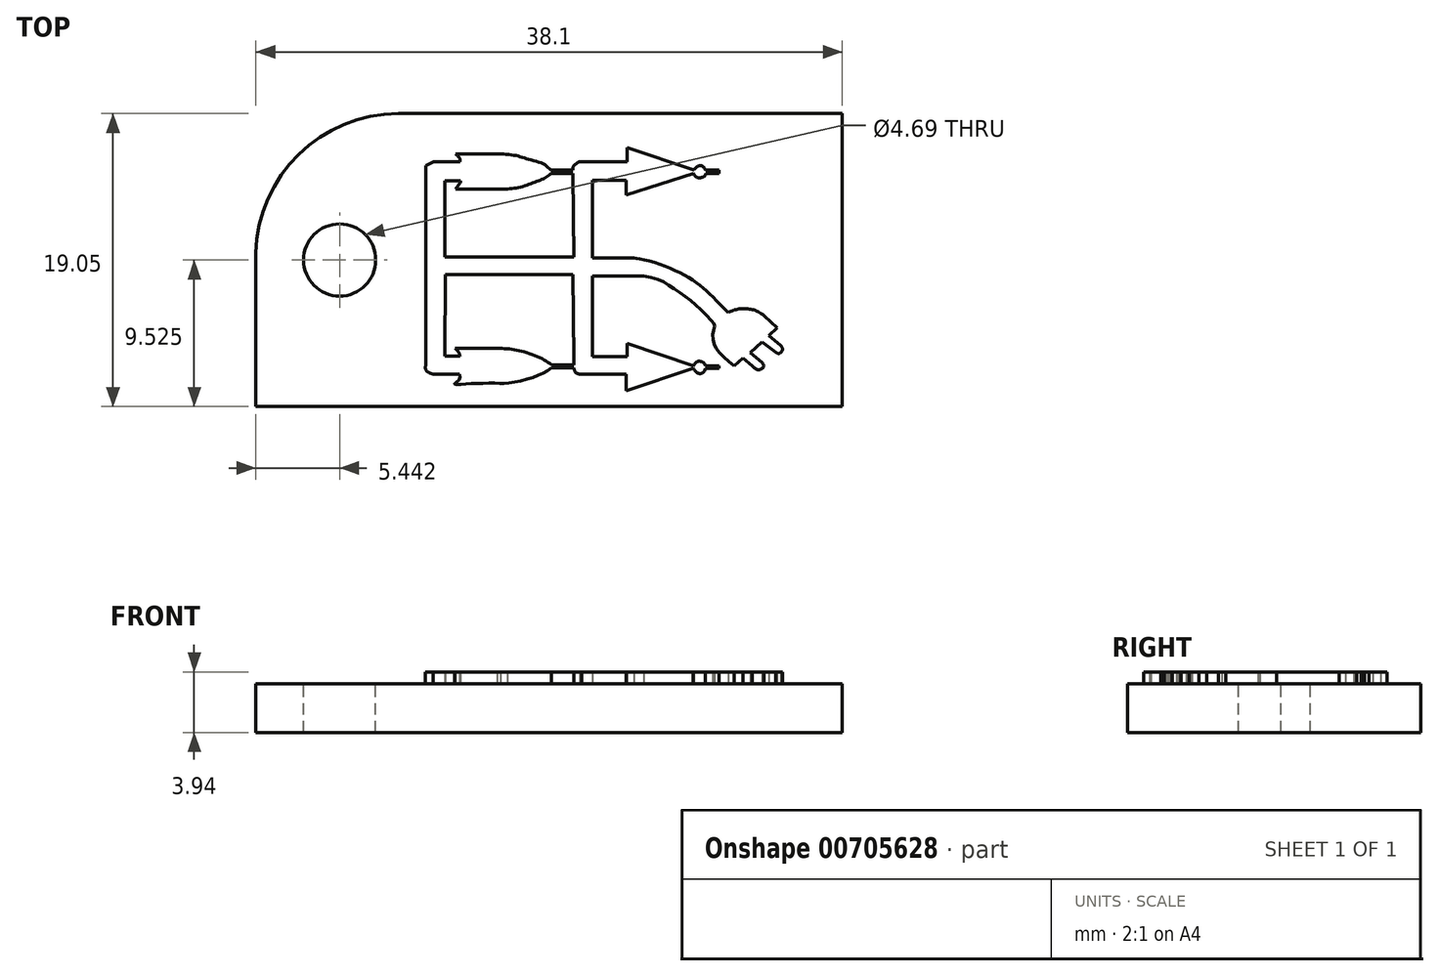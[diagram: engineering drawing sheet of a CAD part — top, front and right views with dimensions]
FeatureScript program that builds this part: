
annotation { "Feature Type Name" : "Feature", "Feature Type Description" : "" }
export const myFeature = defineFeature(function(context is Context, id is Id, definition is map)
    precondition{}
    {
        {
            var Q0;
            Q0=qCreatedBy(makeId("Top.planeOp"),FACE);
            var sketch = newSketch(context, id + "F0", { "sketchPlane" : qUnion([Q0])});
            skLineSegment(sketch, "E0.bottom", {"start": v(0, 0) * mm, "end": v(-38.1, 0) * mm});
            skLineSegment(sketch, "E0.top", {"start": v(0, 19.05) * mm, "end": v(-38.1, 19.05) * mm});
            skLineSegment(sketch, "E0.left", {"start": v(0, 0) * mm, "end": v(0, 19.05) * mm});
            skLineSegment(sketch, "E0.right", {"start": v(-38.1, 0) * mm, "end": v(-38.1, 19.05) * mm});
            skSolve(sketch);
        }
        {
            var Q0;
            Q0=makeQuery(id+"F0.imprint","IMPRINT",FACE,{"disambiguationData":[TD([[makeQuery(id+"F0.imprint","IMPRINT",EDGE,{"derivedFrom":sQuery(id+"F0.wireOp",EDGE,"E0.bottom")}),-1.0]])]});
            extrude(context, id + "F1", {"entities" : qUnion([Q0]), "depth" : 3.17 * mm, "offsetDistance" : 25.4 * mm});
        }
        {
            var Q0;
            Q0=makeQuery(id+"F1.opExtrude","CAP_FACE",FACE,{"disambiguationData":[OSD([sQuery(id+"F0.wireOp",EDGE,"E0.bottom"),sQuery(id+"F0.wireOp",EDGE,"E0.top"),sQuery(id+"F0.wireOp",EDGE,"E0.left"),sQuery(id+"F0.wireOp",EDGE,"E0.right")])],"isStart":false});
            var sketch = newSketch(context, id + "F2", { "sketchPlane" : qUnion([Q0])});
            skLineSegment(sketch, "E1", {"start": v(-38.1, 9.52) * mm, "end": v(0, 9.53) * mm, "construction": true});
            skArc(sketch, "E2", {"start": v(-28.83, 19.05) * mm, "mid": v(-35.46, 16.24) * mm, "end": v(-38.1, 9.52) * mm});
            skArc(sketch, "E3.MirrorCS", {"start": v(-28.83, 0) * mm, "mid": v(-35.46, 2.81) * mm, "end": v(-38.1, 9.52) * mm});
            skCircle(sketch, "E4", {"center": v(-32.66, 9.52) * mm, "radius": 2.35 * mm});
            skSolve(sketch);
        }
        {
            var Q0;
            Q0 = qSketchRegion(id + "F2", true);
            var Q1;
            {var subQ0=sQuery(id+"F2.wireOp",EDGE,"E2");var subQ1=makeQuery(id+"F1.opExtrude","CAP_EDGE",EDGE,{"disambiguationData":[OSD([sQuery(id+"F0.wireOp",EDGE,"E0.top")])],"isStart":false});var subQ2=makeQuery(id+"F2.imprint","INTERSECT",VERTEX,{"derivedFrom":[subQ1,subQ0]});Q1=makeQuery(id+"F2.imprint","IMPRINT",FACE,{"disambiguationData":[TD([[makeQuery(id+"F2.imprint","IMPRINT",EDGE,{"disambiguationData":[TD([[subQ2,-1.0]])],"derivedFrom":subQ0}),-1.0]])]});}
            var Q2;
            {var subQ0=sQuery(id+"F2.wireOp",EDGE,"E3.MirrorCS");var subQ1=makeQuery(id+"F1.opExtrude","CAP_EDGE",EDGE,{"disambiguationData":[OSD([sQuery(id+"F0.wireOp",EDGE,"E0.bottom")])],"isStart":false});var subQ2=makeQuery(id+"F2.imprint","INTERSECT",VERTEX,{"derivedFrom":[subQ1,subQ0]});Q2=makeQuery(id+"F2.imprint","IMPRINT",FACE,{"disambiguationData":[TD([[makeQuery(id+"F2.imprint","IMPRINT",EDGE,{"disambiguationData":[TD([[subQ2,-1.0]])],"derivedFrom":subQ0}),1.0]])]});}
            extrude(context, id + "F3", {"entities" : qUnion([Q0, Q1, Q2]), "operationType" : NewBodyOperationType.REMOVE, "endBound" : BoundingType.THROUGH_ALL, "oppositeDirection" : true, "depth" : 25.4 * mm, "offsetDistance" : 25.4 * mm});
        }
        {
            var Q0;
            Q0=makeQuery(id+"F1.opExtrude","CAP_FACE",FACE,{"disambiguationData":[OSD([sQuery(id+"F0.wireOp",EDGE,"E0.bottom"),sQuery(id+"F0.wireOp",EDGE,"E0.top"),sQuery(id+"F0.wireOp",EDGE,"E0.left"),sQuery(id+"F0.wireOp",EDGE,"E0.right")])],"isStart":false});
            var sketch = newSketch(context, id + "F4", { "sketchPlane" : qUnion([Q0])});
            skLineSegment(sketch, "E5", {"start": v(-27.06, 15.65) * mm, "end": v(-27.06, 2.74) * mm});
            skFitSpline(sketch, "E6", {"points": [v(-27.06, 2.74) * mm, v(-27.06, 2.38) * mm, v(-26.83, 2.2) * mm, v(-26.58, 2.1) * mm], "startDerivative": vector(-0.19, -1.08) * mm, "endDerivative": vector(0.78, -0.26) * mm});
            skLineSegment(sketch, "E7", {"start": v(-26.58, 2.1) * mm, "end": v(-24.87, 2.1) * mm});
            skFitSpline(sketch, "E8", {"points": [v(-24.87, 2.1) * mm, v(-24.87, 1.81) * mm, v(-25.07, 1.59) * mm, v(-25.2, 1.45) * mm, v(-24.7, 1.45) * mm, v(-23.76, 1.5) * mm, v(-22.58, 1.52) * mm, v(-21.85, 1.52) * mm, v(-20.72, 1.7) * mm, v(-19.58, 2.1) * mm, v(-18.9, 2.5) * mm], "startDerivative": vector(0.74, -4.65) * mm, "endDerivative": vector(5.73, 3.88) * mm});
            skLineSegment(sketch, "E9", {"start": v(-18.9, 2.5) * mm, "end": v(-17.45, 2.5) * mm});
            skFitSpline(sketch, "E10", {"points": [v(-17.45, 2.5) * mm, v(-17.3, 2.2) * mm, v(-16.93, 2.1) * mm], "startDerivative": vector(0.18, -0.76) * mm, "endDerivative": vector(0.85, -0.08) * mm});
            skLineSegment(sketch, "E11", {"start": v(-16.93, 2.1) * mm, "end": v(-14.03, 2.1) * mm});
            skLineSegment(sketch, "E12", {"start": v(-14.03, 2.1) * mm, "end": v(-14.03, 1.02) * mm});
            skLineSegment(sketch, "E13", {"start": v(-14.03, 1.02) * mm, "end": v(-9.68, 2.5) * mm});
            skFitSpline(sketch, "E14", {"points": [v(-9.68, 2.5) * mm, v(-9.55, 2.3) * mm, v(-9.36, 2.16) * mm, v(-9.15, 2.15) * mm, v(-8.98, 2.27) * mm, v(-8.89, 2.5) * mm], "startDerivative": vector(0.59, -1) * mm, "endDerivative": vector(0.34, 1.16) * mm});
            skLineSegment(sketch, "E15", {"start": v(-8.89, 2.5) * mm, "end": v(-8, 2.5) * mm});
            skLineSegment(sketch, "E16", {"start": v(-8, 2.5) * mm, "end": v(-8, 2.65) * mm});
            skLineSegment(sketch, "E17", {"start": v(-8, 2.65) * mm, "end": v(-8.89, 2.65) * mm});
            skFitSpline(sketch, "E18", {"points": [v(-8.89, 2.65) * mm, v(-9.03, 2.86) * mm, v(-9.23, 2.94) * mm, v(-9.42, 2.93) * mm, v(-9.56, 2.8) * mm, v(-9.65, 2.65) * mm], "startDerivative": vector(-0.56, 1.07) * mm, "endDerivative": vector(-0.46, -0.78) * mm});
            skLineSegment(sketch, "E19", {"start": v(-9.65, 2.65) * mm, "end": v(-13.98, 4.11) * mm});
            skLineSegment(sketch, "E20", {"start": v(-13.98, 4.11) * mm, "end": v(-13.98, 3.24) * mm});
            skLineSegment(sketch, "E21", {"start": v(-13.98, 3.24) * mm, "end": v(-16.22, 3.24) * mm});
            skLineSegment(sketch, "E22", {"start": v(-16.22, 3.24) * mm, "end": v(-16.22, 8.47) * mm});
            skLineSegment(sketch, "E23", {"start": v(-16.22, 8.47) * mm, "end": v(-12.88, 8.47) * mm});
            skFitSpline(sketch, "E24", {"points": [v(-12.88, 8.47) * mm, v(-11.76, 8.17) * mm, v(-10.96, 7.67) * mm, v(-10.07, 7.06) * mm, v(-9.23, 6.32) * mm, v(-8.41, 5.48) * mm, v(-8.28, 5.26) * mm, v(-8.38, 4.97) * mm, v(-8.4, 4.4) * mm, v(-8.28, 3.92) * mm, v(-7.84, 3.37) * mm, v(-7.02, 2.63) * mm], "startDerivative": vector(10.66, -2.14) * mm, "endDerivative": vector(7.96, -6.93) * mm});
            skLineSegment(sketch, "E25", {"start": v(-7.02, 2.63) * mm, "end": v(-6.45, 3.14) * mm});
            skLineSegment(sketch, "E26", {"start": v(-6.45, 3.14) * mm, "end": v(-5.85, 2.63) * mm});
            skFitSpline(sketch, "E27", {"points": [v(-5.85, 2.63) * mm, v(-5.56, 2.4) * mm, v(-5.31, 2.4) * mm, v(-5.1, 2.63) * mm, v(-5.22, 2.86) * mm], "startDerivative": vector(1.01, -1) * mm, "endDerivative": vector(-0.8, 0.95) * mm});
            skLineSegment(sketch, "E28", {"start": v(-5.22, 2.86) * mm, "end": v(-5.98, 3.49) * mm});
            skLineSegment(sketch, "E29", {"start": v(-5.98, 3.49) * mm, "end": v(-5.22, 4.2) * mm});
            skLineSegment(sketch, "E30", {"start": v(-5.22, 4.2) * mm, "end": v(-4.34, 3.52) * mm});
            skFitSpline(sketch, "E31", {"points": [v(-4.34, 3.52) * mm, v(-4.13, 3.45) * mm, v(-3.92, 3.6) * mm, v(-3.9, 3.82) * mm, v(-4, 3.98) * mm], "startDerivative": vector(0.8, -0.5) * mm, "endDerivative": vector(-0.48, 0.65) * mm});
            skLineSegment(sketch, "E32", {"start": v(-4, 3.98) * mm, "end": v(-4.78, 4.61) * mm});
            skLineSegment(sketch, "E33", {"start": v(-4.78, 4.61) * mm, "end": v(-4.23, 5.12) * mm});
            skLineSegment(sketch, "E34", {"start": v(-4.23, 5.12) * mm, "end": v(-5.06, 5.89) * mm});
            skFitSpline(sketch, "E35", {"points": [v(-5.06, 5.89) * mm, v(-5.57, 6.21) * mm, v(-5.97, 6.32) * mm, v(-6.46, 6.35) * mm, v(-6.95, 6.3) * mm, v(-7.4, 6.1) * mm], "startDerivative": vector(-2.38, 1.67) * mm, "endDerivative": vector(-2.24, -1.1) * mm});
            skFitSpline(sketch, "E36", {"points": [v(-7.4, 6.1) * mm, v(-8.54, 7.24) * mm, v(-9.34, 7.95) * mm, v(-10.44, 8.63) * mm, v(-11.92, 9.27) * mm, v(-13.3, 9.63) * mm, v(-13.65, 9.68) * mm], "startDerivative": vector(-6.1, 6.2) * mm, "endDerivative": vector(-3.18, 0.53) * mm});
            skLineSegment(sketch, "E37", {"start": v(-13.55, 9.67) * mm, "end": v(-16.23, 9.67) * mm});
            skLineSegment(sketch, "E38", {"start": v(-16.23, 9.67) * mm, "end": v(-16.23, 14.71) * mm});
            skLineSegment(sketch, "E39", {"start": v(-16.23, 14.71) * mm, "end": v(-14.04, 14.71) * mm});
            skLineSegment(sketch, "E40", {"start": v(-14.04, 14.71) * mm, "end": v(-14.04, 13.75) * mm});
            skLineSegment(sketch, "E41", {"start": v(-14.04, 13.75) * mm, "end": v(-9.66, 15.16) * mm});
            skFitSpline(sketch, "E42", {"points": [v(-9.66, 15.16) * mm, v(-9.41, 14.88) * mm, v(-8.96, 14.97) * mm, v(-8.87, 15.16) * mm], "startDerivative": vector(0.54, -1.03) * mm, "endDerivative": vector(0.13, 0.78) * mm});
            skLineSegment(sketch, "E43", {"start": v(-8.87, 15.16) * mm, "end": v(-8, 15.16) * mm});
            skLineSegment(sketch, "E44", {"start": v(-8, 15.16) * mm, "end": v(-8, 15.37) * mm});
            skLineSegment(sketch, "E45", {"start": v(-8, 15.37) * mm, "end": v(-8.87, 15.37) * mm});
            skFitSpline(sketch, "E46", {"points": [v(-8.87, 15.37) * mm, v(-9.05, 15.6) * mm, v(-9.28, 15.66) * mm, v(-9.56, 15.5) * mm, v(-9.65, 15.31) * mm], "startDerivative": vector(-0.6, 0.94) * mm, "endDerivative": vector(-0.32, -0.8) * mm});
            skLineSegment(sketch, "E47", {"start": v(-9.63, 15.37) * mm, "end": v(-13.97, 16.83) * mm});
            skLineSegment(sketch, "E48", {"start": v(-13.97, 16.83) * mm, "end": v(-13.97, 15.93) * mm});
            skLineSegment(sketch, "E49", {"start": v(-13.97, 15.93) * mm, "end": v(-17.07, 15.93) * mm});
            skFitSpline(sketch, "E50", {"points": [v(-17.07, 15.93) * mm, v(-17.47, 15.61) * mm, v(-17.5, 15.36) * mm], "startDerivative": vector(-0.87, -0.5) * mm, "endDerivative": vector(0.05, -0.62) * mm});
            skLineSegment(sketch, "E51", {"start": v(-17.5, 15.36) * mm, "end": v(-18.94, 15.36) * mm});
            skFitSpline(sketch, "E52", {"points": [v(-18.94, 15.36) * mm, v(-19.41, 15.77) * mm, v(-20.41, 16.08) * mm, v(-21.13, 16.3) * mm, v(-22.2, 16.43) * mm], "startDerivative": vector(-1.83, 2.1) * mm, "endDerivative": vector(-4.1, 0.3) * mm});
            skLineSegment(sketch, "E53", {"start": v(-22.2, 16.43) * mm, "end": v(-25.13, 16.43) * mm});
            skFitSpline(sketch, "E54", {"points": [v(-25.13, 16.43) * mm, v(-24.85, 16.12) * mm, v(-24.83, 15.91) * mm], "startDerivative": vector(0.6, -0.53) * mm, "endDerivative": vector(-0.02, -0.5) * mm});
            skLineSegment(sketch, "E55", {"start": v(-24.83, 15.91) * mm, "end": v(-26.54, 15.91) * mm});
            skFitSpline(sketch, "E56", {"points": [v(-26.54, 15.91) * mm, v(-27.06, 15.65) * mm], "startDerivative": vector(-0.52, -0.26) * mm, "endDerivative": vector(-0.52, -0.26) * mm});
            skLineSegment(sketch, "E57", {"start": v(-17.5, 15.14) * mm, "end": v(-18.93, 15.14) * mm});
            skFitSpline(sketch, "E58", {"points": [v(-18.93, 15.14) * mm, v(-19.43, 14.8) * mm, v(-20.04, 14.57) * mm, v(-20.88, 14.27) * mm, v(-21.75, 14.14) * mm], "startDerivative": vector(-2.16, -1.62) * mm, "endDerivative": vector(-3.23, -0.3) * mm});
            skLineSegment(sketch, "E59", {"start": v(-21.75, 14.14) * mm, "end": v(-25.12, 14.14) * mm});
            skFitSpline(sketch, "E60", {"points": [v(-25.12, 14.14) * mm, v(-24.93, 14.4) * mm, v(-24.8, 14.6) * mm, v(-24.8, 14.72) * mm], "startDerivative": vector(0.45, 0.65) * mm, "endDerivative": vector(-0.08, 0.44) * mm});
            skLineSegment(sketch, "E61", {"start": v(-24.8, 14.68) * mm, "end": v(-25.82, 14.68) * mm});
            skLineSegment(sketch, "E62", {"start": v(-25.82, 14.68) * mm, "end": v(-25.82, 9.71) * mm});
            skLineSegment(sketch, "E63", {"start": v(-25.82, 9.71) * mm, "end": v(-17.43, 9.71) * mm});
            skLineSegment(sketch, "E64", {"start": v(-17.43, 9.71) * mm, "end": v(-17.5, 15.14) * mm});
            skLineSegment(sketch, "E65", {"start": v(-25.8, 8.58) * mm, "end": v(-17.5, 8.58) * mm});
            skLineSegment(sketch, "E66", {"start": v(-17.5, 8.58) * mm, "end": v(-17.45, 3.15) * mm});
            skLineSegment(sketch, "E67", {"start": v(-17.45, 3.15) * mm, "end": v(-17.45, 2.71) * mm});
            skLineSegment(sketch, "E68", {"start": v(-17.45, 2.71) * mm, "end": v(-18.86, 2.71) * mm});
            skFitSpline(sketch, "E69", {"points": [v(-18.86, 2.71) * mm, v(-19.56, 3.13) * mm, v(-20.6, 3.53) * mm, v(-21.56, 3.73) * mm, v(-22.42, 3.8) * mm], "startDerivative": vector(-2.8, 1.85) * mm, "endDerivative": vector(-3.56, 0.15) * mm});
            skLineSegment(sketch, "E70", {"start": v(-22.42, 3.8) * mm, "end": v(-25.16, 3.8) * mm});
            skFitSpline(sketch, "E71", {"points": [v(-25.16, 3.8) * mm, v(-24.92, 3.51) * mm, v(-24.84, 3.27) * mm], "startDerivative": vector(0.5, -0.5) * mm, "endDerivative": vector(0.12, -0.53) * mm});
            skLineSegment(sketch, "E72", {"start": v(-24.84, 3.27) * mm, "end": v(-25.82, 3.27) * mm});
            skLineSegment(sketch, "E73", {"start": v(-25.82, 3.27) * mm, "end": v(-25.8, 8.58) * mm});
            skLineSegment(sketch, "E74", {"start": v(-13.55, 9.67) * mm, "end": v(-13.55, 9.67) * mm});
            skSolve(sketch);
        }
        {
            var Q0;
            Q0=makeQuery(id+"F4.imprint","IMPRINT",FACE,{"disambiguationData":[TD([[makeQuery(id+"F4.imprint","IMPRINT",EDGE,{"derivedFrom":sQuery(id+"F4.wireOp",EDGE,"E5")}),1.0]])]});
            extrude(context, id + "F5", {"entities" : qUnion([Q0]), "operationType" : NewBodyOperationType.ADD, "depth" : 0.76 * mm, "offsetDistance" : 25.4 * mm});
        }
    });
